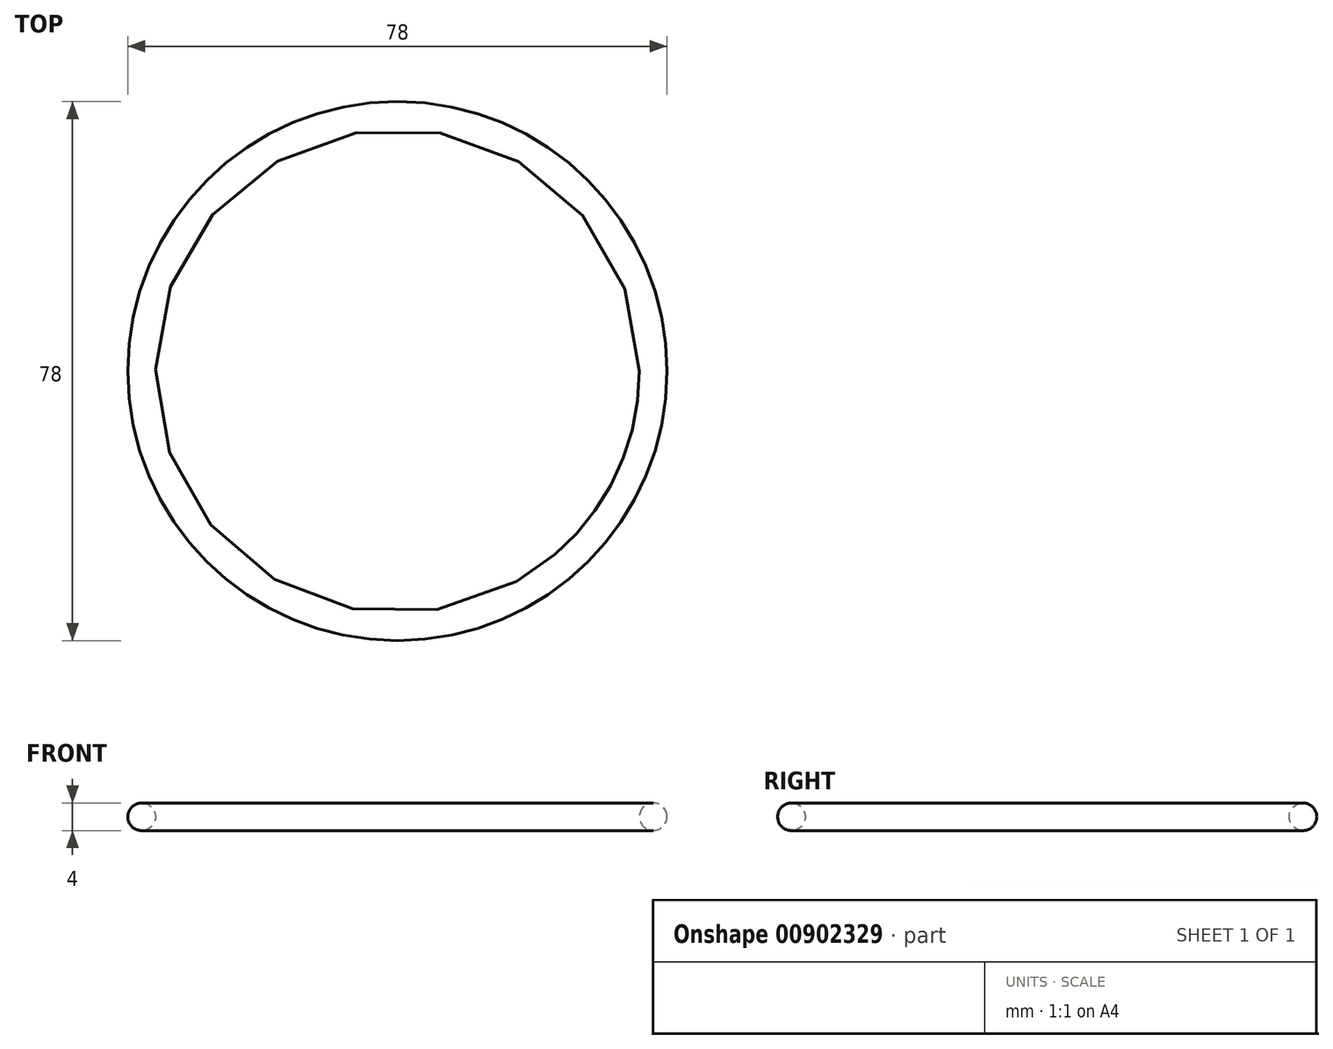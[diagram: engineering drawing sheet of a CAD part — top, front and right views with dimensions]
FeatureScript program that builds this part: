
annotation { "Feature Type Name" : "Feature", "Feature Type Description" : "" }
export const myFeature = defineFeature(function(context is Context, id is Id, definition is map)
    precondition{}
    {
        {
            var Q0;
            Q0=qCreatedBy(makeId("Top.planeOp"),FACE);
            var sketch = newSketch(context, id + "F0", { "sketchPlane" : qUnion([Q0])});
            skCircle(sketch, "E0", {"center": v(0, 0) * mm, "radius": 39 * mm});
            skCircle(sketch, "E1", {"center": v(0, 0) * mm, "radius": 35 * mm});
            skSolve(sketch);
        }
        {
            var Q0;
            Q0=qSketchRegion(id+"F0",true);
            extrude(context, id + "F1", {"entities" : qUnion([Q0]), "depth" : 4 * mm, "offsetDistance" : 25 * mm});
        }
        {
            var Q0;
            Q0=makeQuery(id+"F1.opExtrude","CAP_FACE",FACE,{"disambiguationData":[OSD([sQuery(id+"F0.wireOp",EDGE,"E0"),sQuery(id+"F0.wireOp",EDGE,"E1")])],"isStart":true});
            fillet(context, id + "F2", {"entities" : qUnion([Q0]), "radius" : 2 * mm, "tangentPropagation" : true, "allowEdgeOverflow" : false});
        }
        {
            var Q0;
            Q0=makeQuery(id+"F1.opExtrude","CAP_FACE",FACE,{"disambiguationData":[OSD([sQuery(id+"F0.wireOp",EDGE,"E0"),sQuery(id+"F0.wireOp",EDGE,"E1")])],"isStart":false});
            fillet(context, id + "F3", {"entities" : qUnion([Q0]), "radius" : 2 * mm, "tangentPropagation" : true, "allowEdgeOverflow" : false});
        }
        {
            var Q0;
            Q0=qCreatedBy(makeId("Top.planeOp"),FACE);
            cPlane(context, id + "F4", {"entities" : qUnion([Q0]), "cplaneType" : CPlaneType.OFFSET, "offset" : 2 * mm, "width" : 150 * mm, "height" : 150 * mm});
        }
    });
